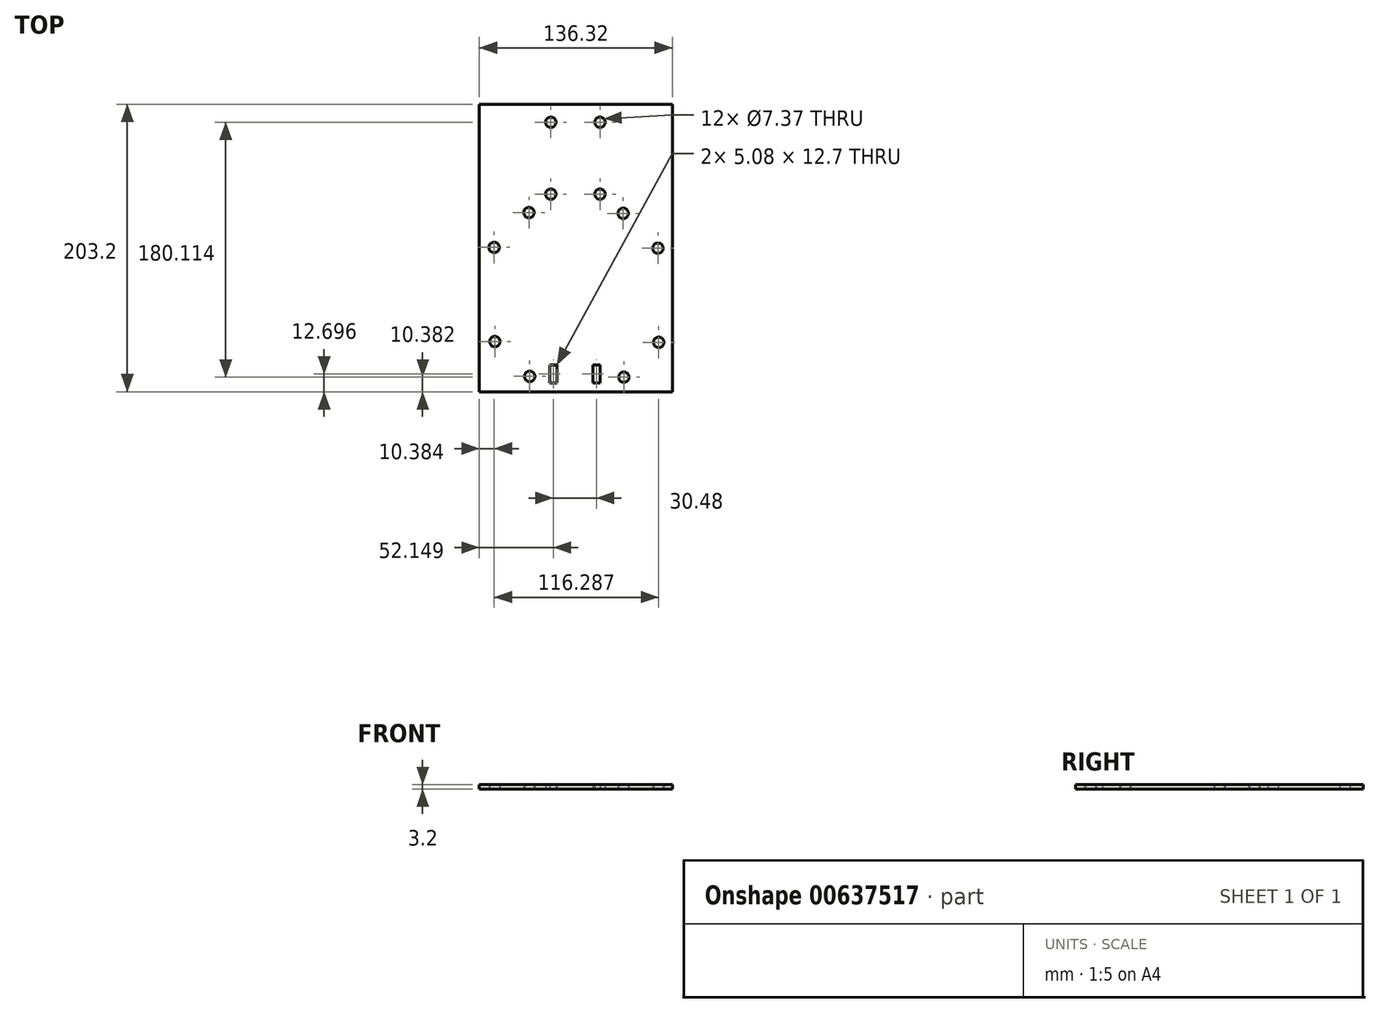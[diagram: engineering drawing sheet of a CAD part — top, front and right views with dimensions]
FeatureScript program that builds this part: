
annotation { "Feature Type Name" : "Feature", "Feature Type Description" : "" }
export const myFeature = defineFeature(function(context is Context, id is Id, definition is map)
    precondition{}
    {
        {
            var Q0;
            Q0=qCreatedBy(makeId("Top.planeOp"),FACE);
            var sketch = newSketch(context, id + "F0", { "sketchPlane" : qUnion([Q0])});
            skLineSegment(sketch, "E0.bottom", {"start": v(-67.81, 127.52) * mm, "end": v(68.51, 127.52) * mm});
            skLineSegment(sketch, "E0.top", {"start": v(-67.81, -75.68) * mm, "end": v(68.51, -75.68) * mm});
            skLineSegment(sketch, "E0.left", {"start": v(-67.81, 127.52) * mm, "end": v(-67.81, -75.68) * mm});
            skLineSegment(sketch, "E0.right", {"start": v(68.51, 127.52) * mm, "end": v(68.51, -75.68) * mm});
            skLineSegment(sketch, "E1.8", {"start": v(-68.01, -75.68) * mm, "end": v(68.51, -75.68) * mm, "construction": true});
            skLineSegment(sketch, "E2.bottom", {"start": v(17.36, -69.33) * mm, "end": v(12.28, -69.33) * mm});
            skLineSegment(sketch, "E2.top", {"start": v(17.36, -56.63) * mm, "end": v(12.28, -56.63) * mm});
            skLineSegment(sketch, "E2.left", {"start": v(17.36, -69.33) * mm, "end": v(17.36, -56.63) * mm});
            skLineSegment(sketch, "E2.right", {"start": v(12.28, -69.33) * mm, "end": v(12.28, -56.63) * mm});
            skPoint(sketch, "E2.middle", {"position": v(14.82, -62.98) * mm});
            skLineSegment(sketch, "E3.MirrorCS", {"start": v(-18.2, -56.63) * mm, "end": v(-13.12, -56.63) * mm});
            skLineSegment(sketch, "E4.MirrorCS", {"start": v(-13.12, -69.33) * mm, "end": v(-13.12, -56.63) * mm});
            skLineSegment(sketch, "E5.MirrorCS", {"start": v(-18.2, -69.33) * mm, "end": v(-18.2, -56.63) * mm});
            skLineSegment(sketch, "E6.MirrorCS", {"start": v(-18.2, -69.33) * mm, "end": v(-13.12, -69.33) * mm});
            skLineSegment(sketch, "E7.0", {"start": v(52.14, -35.8) * mm, "end": v(52.14, -35.8) * mm});
            skLineSegment(sketch, "E7.1", {"start": v(12.28, -69.33) * mm, "end": v(12.28, -56.63) * mm, "construction": true});
            skCircle(sketch, "E8", {"center": v(58.86, -40.7) * mm, "radius": 3.68 * mm});
            skCircle(sketch, "E9.MirrorC", {"center": v(34.26, -65.3) * mm, "radius": 3.68 * mm});
            skCircle(sketch, "E10.MirrorC", {"center": v(-57.43, 26.38) * mm, "radius": 3.68 * mm});
            skCircle(sketch, "E11.MirrorC", {"center": v(-32.82, 50.99) * mm, "radius": 3.68 * mm});
            skCircle(sketch, "E12.MirrorC", {"center": v(-56.9, -40.16) * mm, "radius": 3.68 * mm});
            skCircle(sketch, "E13.MirrorC", {"center": v(-32.29, -64.76) * mm, "radius": 3.68 * mm});
            skCircle(sketch, "E14.MirrorC", {"center": v(33.72, 50.46) * mm, "radius": 3.68 * mm});
            skCircle(sketch, "E15.MirrorC", {"center": v(58.33, 25.85) * mm, "radius": 3.68 * mm});
            skCircle(sketch, "E16.MirrorC", {"center": v(17.4, 114.82) * mm, "radius": 3.68 * mm});
            skCircle(sketch, "E17.MirrorC", {"center": v(17.4, 64.02) * mm, "radius": 3.68 * mm});
            skCircle(sketch, "E18.MirrorC", {"center": v(-17.4, 64.02) * mm, "radius": 3.68 * mm});
            skCircle(sketch, "E19.MirrorC", {"center": v(-17.4, 114.82) * mm, "radius": 3.68 * mm});
            skSolve(sketch);
        }
        {
            var Q0;
            Q0=makeQuery(id+"F0.imprint","IMPRINT",FACE,{"disambiguationData":[TD([[makeQuery(id+"F0.imprint","IMPRINT",EDGE,{"derivedFrom":sQuery(id+"F0.wireOp",EDGE,"E0.bottom")}),-1.0]])]});
            extrude(context, id + "F1", {"entities" : qUnion([Q0]), "depth" : 3.2 * mm, "offsetDistance" : 25.4 * mm});
        }
    });
